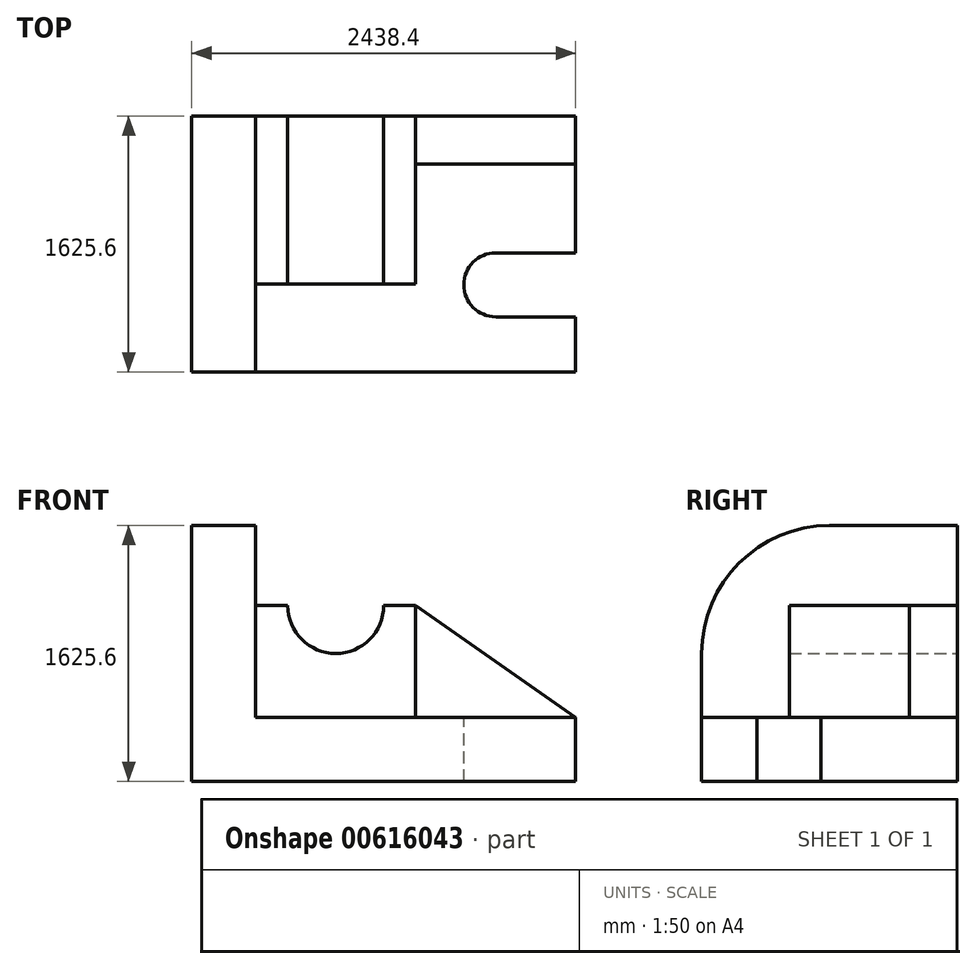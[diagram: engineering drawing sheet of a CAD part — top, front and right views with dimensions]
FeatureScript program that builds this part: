
annotation { "Feature Type Name" : "Feature", "Feature Type Description" : "" }
export const myFeature = defineFeature(function(context is Context, id is Id, definition is map)
    precondition{}
    {
        {
            var Q0;
            Q0=qCreatedBy(makeId("Top.planeOp"),FACE);
            var sketch = newSketch(context, id + "F0", { "sketchPlane" : qUnion([Q0])});
            skLineSegment(sketch, "E0.bottom", {"start": v(-1181.05, 810.48) * mm, "end": v(1257.35, 810.48) * mm});
            skLineSegment(sketch, "E0.top", {"start": v(-1181.05, -815.12) * mm, "end": v(1257.35, -815.12) * mm});
            skLineSegment(sketch, "E0.left", {"start": v(-1181.05, 810.48) * mm, "end": v(-1181.05, -815.12) * mm});
            skLineSegment(sketch, "E0.right", {"start": v(1257.35, 810.48) * mm, "end": v(1257.35, -815.12) * mm});
            skSolve(sketch);
        }
        {
            var Q0;
            Q0 = qSketchRegion(id + "F0", true);
            extrude(context, id + "F1", {"entities" : qUnion([Q0]), "depth" : 406.4 * mm, "offsetDistance" : 25.4 * mm});
        }
        {
            var Q0;
            Q0=makeQuery(id+"F1.opExtrude","SWEPT_FACE",FACE,{"disambiguationData":[OSD([sQuery(id+"F0.wireOp",EDGE,"E0.left")])]});
            var sketch = newSketch(context, id + "F2", { "sketchPlane" : qUnion([Q0])});
            skLineSegment(sketch, "E1.bottom", {"start": v(-810.48, 0) * mm, "end": v(815.12, 0) * mm});
            skLineSegment(sketch, "E1.top", {"start": v(-810.48, 1625.6) * mm, "end": v(815.12, 1625.6) * mm});
            skLineSegment(sketch, "E1.left", {"start": v(-810.48, 0) * mm, "end": v(-810.48, 1625.6) * mm});
            skLineSegment(sketch, "E1.right", {"start": v(815.12, 0) * mm, "end": v(815.12, 1625.6) * mm});
            skSolve(sketch);
        }
        {
            var Q0;
            Q0 = qSketchRegion(id + "F2", true);
            extrude(context, id + "F3", {"entities" : qUnion([Q0]), "operationType" : NewBodyOperationType.ADD, "oppositeDirection" : true, "depth" : 406.4 * mm, "offsetDistance" : 25.4 * mm});
        }
        {
            var Q0;
            Q0=makeQuery(id+"F1.opExtrude","CAP_FACE",FACE,{"disambiguationData":[OSD([sQuery(id+"F0.wireOp",EDGE,"E0.bottom"),sQuery(id+"F0.wireOp",EDGE,"E0.top"),sQuery(id+"F0.wireOp",EDGE,"E0.left"),sQuery(id+"F0.wireOp",EDGE,"E0.right")])],"isStart":false});
            var sketch = newSketch(context, id + "F4", { "sketchPlane" : qUnion([Q0])});
            skLineSegment(sketch, "E2.bottom", {"start": v(-774.65, 810.48) * mm, "end": v(241.35, 810.48) * mm});
            skLineSegment(sketch, "E2.top", {"start": v(-774.65, -256.32) * mm, "end": v(241.35, -256.32) * mm});
            skLineSegment(sketch, "E2.left", {"start": v(-774.65, 810.48) * mm, "end": v(-774.65, -256.32) * mm});
            skLineSegment(sketch, "E2.right", {"start": v(241.35, 810.48) * mm, "end": v(241.35, -256.32) * mm});
            skSolve(sketch);
        }
        {
            var Q0;
            Q0=makeQuery(id+"F4.imprint","IMPRINT",FACE,{"disambiguationData":[TD([[makeQuery(id+"F4.imprint","IMPRINT",EDGE,{"derivedFrom":sQuery(id+"F4.wireOp",EDGE,"E2.bottom")}),-1.0]])]});
            extrude(context, id + "F5", {"entities" : qUnion([Q0]), "operationType" : NewBodyOperationType.ADD, "depth" : 711.2 * mm, "offsetDistance" : 25.4 * mm});
        }
        {
            var Q0;
            Q0=makeQuery(id+"F5.opExtrude","SWEPT_FACE",FACE,{"disambiguationData":[OSD([sQuery(id+"F4.wireOp",EDGE,"E2.top")])]});
            var sketch = newSketch(context, id + "F6", { "sketchPlane" : qUnion([Q0])});
            skCircle(sketch, "E3", {"center": v(-266.65, 1117.6) * mm, "radius": 304.8 * mm});
            skSolve(sketch);
        }
        {
            var Q0;
            {var subQ0=sQuery(id+"F6.wireOp",EDGE,"E3");var subQ1=makeQuery(id+"F5.opExtrude","CAP_EDGE",EDGE,{"disambiguationData":[OSD([sQuery(id+"F4.wireOp",EDGE,"E2.top")])],"isStart":false});var subQ2=makeQuery(id+"F6.imprint","INTERSECT",VERTEX,{"disambiguationData":[OD(0.0)],"derivedFrom":[subQ1,subQ0]});Q0=makeQuery(id+"F6.imprint","IMPRINT",FACE,{"disambiguationData":[TD([[makeQuery(id+"F6.imprint","IMPRINT",EDGE,{"disambiguationData":[TD([[subQ2,1.0]])],"derivedFrom":subQ0}),1.0]])]});}
            var Q1;
            Q1=makeQuery(id+"F5.opExtrude","CAP_EDGE",EDGE,{"disambiguationData":[OSD([sQuery(id+"F4.wireOp",EDGE,"E2.right")])],"isStart":false});
            sweep(context, id + "F7", {"operationType" : NewBodyOperationType.REMOVE, "profiles" : qUnion([Q0]), "path" : qUnion([Q1])});
        }
        {
            var Q0;
            Q0=makeQuery(id+"F3.opExtrude","SWEPT_EDGE",EDGE,{"disambiguationData":[OSD([sQuery(id+"F2.wireOp",EDGE,"E1.top"),sQuery(id+"F2.wireOp",EDGE,"E1.right")])]});
            fillet(context, id + "F8", {"entities" : qUnion([Q0]), "radius" : 812.8 * mm, "tangentPropagation" : true, "allowEdgeOverflow" : false});
        }
        {
            var Q0;
            Q0=makeQuery(id+"F5.opExtrude","SWEPT_FACE",FACE,{"disambiguationData":[OSD([sQuery(id+"F4.wireOp",EDGE,"E2.right")])]});
            var sketch = newSketch(context, id + "F9", { "sketchPlane" : qUnion([Q0])});
            skLineSegment(sketch, "E4.bottom", {"start": v(810.48, 1117.6) * mm, "end": v(505.68, 1117.6) * mm});
            skLineSegment(sketch, "E4.top", {"start": v(810.48, 406.4) * mm, "end": v(505.68, 406.4) * mm});
            skLineSegment(sketch, "E4.left", {"start": v(810.48, 1117.6) * mm, "end": v(810.48, 406.4) * mm});
            skLineSegment(sketch, "E4.right", {"start": v(505.68, 1117.6) * mm, "end": v(505.68, 406.4) * mm});
            skSolve(sketch);
        }
        {
            var Q0;
            Q0 = qSketchRegion(id + "F9", true);
            extrude(context, id + "F10", {"entities" : qUnion([Q0]), "operationType" : NewBodyOperationType.ADD, "depth" : 1016 * mm, "offsetDistance" : 25.4 * mm});
        }
        {
            var Q0;
            Q0=makeQuery(id+"F10.opExtrude","SWEPT_FACE",FACE,{"disambiguationData":[OSD([sQuery(id+"F9.wireOp",EDGE,"E4.right")])]});
            var sketch = newSketch(context, id + "F11", { "sketchPlane" : qUnion([Q0])});
            skLineSegment(sketch, "E5", {"start": v(241.35, 1117.6) * mm, "end": v(1257.35, 406.4) * mm});
            skSolve(sketch);
        }
        {
            var Q0;
            Q0=makeQuery(id+"F11.imprint","IMPRINT",FACE,{"disambiguationData":[TD([[makeQuery(id+"F11.imprint","IMPRINT",EDGE,{"derivedFrom":sQuery(id+"F11.wireOp",EDGE,"E5")}),1.0]])]});
            var Q1;
            Q1=makeQuery(id+"F10.opExtrude","CAP_EDGE",EDGE,{"disambiguationData":[OSD([sQuery(id+"F9.wireOp",EDGE,"E4.bottom")])],"isStart":false});
            sweep(context, id + "F12", {"operationType" : NewBodyOperationType.REMOVE, "profiles" : qUnion([Q0]), "path" : qUnion([Q1])});
        }
        {
            var Q0;
            {var subQ5=sQuery(id+"F4.wireOp",EDGE,"E2.top");Q0=makeQuery(id+"F4.imprint","IMPRINT",FACE,{"disambiguationData":[TD([[makeQuery(id+"F4.imprint","IMPRINT",EDGE,{"derivedFrom":subQ5}),-1.0]])]});}
            var sketch = newSketch(context, id + "F13", { "sketchPlane" : qUnion([Q0])});
            skLineSegment(sketch, "E6.bottom", {"start": v(1257.37, -464.42) * mm, "end": v(749.37, -464.42) * mm});
            skLineSegment(sketch, "E6.top", {"start": v(1257.37, -58.02) * mm, "end": v(749.37, -58.02) * mm});
            skLineSegment(sketch, "E6.left", {"start": v(1257.37, -464.42) * mm, "end": v(1257.37, -58.02) * mm});
            skLineSegment(sketch, "E6.right", {"start": v(749.37, -464.42) * mm, "end": v(749.37, -58.02) * mm});
            skCircle(sketch, "E7", {"center": v(749.37, -261.22) * mm, "radius": 203.2 * mm});
            skSolve(sketch);
        }
        {
            var Q0;
            Q0 = qSketchRegion(id + "F13", true);
            extrude(context, id + "F14", {"entities" : qUnion([Q0]), "operationType" : NewBodyOperationType.REMOVE, "oppositeDirection" : true, "depth" : 574.04 * mm, "offsetDistance" : 25.4 * mm});
        }
    });
